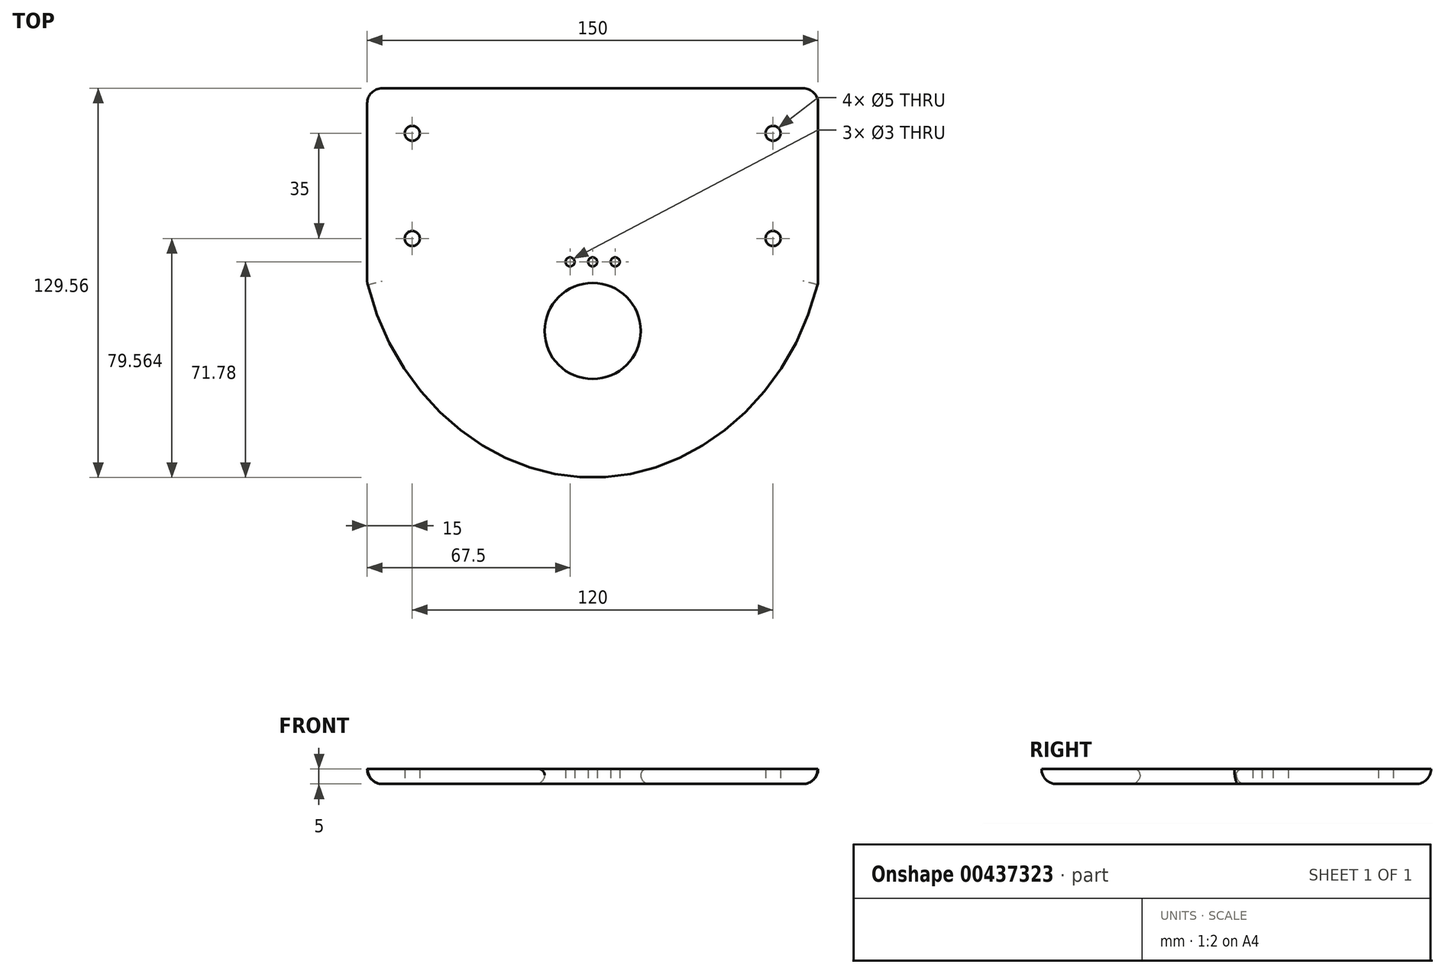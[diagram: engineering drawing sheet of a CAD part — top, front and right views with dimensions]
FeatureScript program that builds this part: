
annotation { "Feature Type Name" : "Feature", "Feature Type Description" : "" }
export const myFeature = defineFeature(function(context is Context, id is Id, definition is map)
    precondition{}
    {
        {
            var Q0;
            Q0=qCreatedBy(makeId("Top.planeOp"),FACE);
            var sketch = newSketch(context, id + "F0", { "sketchPlane" : qUnion([Q0])});
            skLineSegment(sketch, "E0.bottom", {"start": v(75, 64.78) * mm, "end": v(-75, 64.78) * mm});
            skLineSegment(sketch, "E0.top", {"start": v(0, -64.78) * mm, "end": v(0, -64.78) * mm});
            skLineSegment(sketch, "E0.left", {"start": v(75, 64.78) * mm, "end": v(75, 0) * mm});
            skLineSegment(sketch, "E0.right", {"start": v(-75, 64.78) * mm, "end": v(-75, 0) * mm});
            skPoint(sketch, "E0.middle", {"position": v(0, 0) * mm});
            skLineSegment(sketch, "E1", {"start": v(0, 64.78) * mm, "end": v(0, -64.78) * mm, "construction": true});
            skLineSegment(sketch, "E2", {"start": v(-75, 0) * mm, "end": v(100.62, 0) * mm, "construction": true});
            skPoint(sketch, "E2.startSnap0", {"position": v(-75, 0) * mm});
            skPoint(sketch, "E3.orphan", {"position": v(-130.6, 0) * mm});
            skFitSpline(sketch, "E4", {"points": [v(-75, 0) * mm, v(0, -64.78) * mm, v(75, 0) * mm], "startDerivative": vector(60, -240) * mm, "endDerivative": vector(60, 240) * mm});
            skPoint(sketch, "E5.orphan", {"position": v(-75, -64.78) * mm});
            skPoint(sketch, "E6.orphan", {"position": v(75, -64.78) * mm});
            skCircle(sketch, "E7", {"center": v(60, 49.78) * mm, "radius": 2.5 * mm});
            skCircle(sketch, "E8", {"center": v(60, 14.78) * mm, "radius": 2.5 * mm});
            skCircle(sketch, "E9.MirrorC", {"center": v(-60, 14.78) * mm, "radius": 2.5 * mm});
            skCircle(sketch, "E10.MirrorC", {"center": v(-60, 49.78) * mm, "radius": 2.5 * mm});
            skCircle(sketch, "E11", {"center": v(0, 7) * mm, "radius": 1.5 * mm});
            skCircle(sketch, "E12", {"center": v(7.5, 7) * mm, "radius": 1.5 * mm});
            skCircle(sketch, "E13", {"center": v(-7.5, 7) * mm, "radius": 1.5 * mm});
            skSolve(sketch);
        }
        {
            var Q0;
            Q0=makeQuery(id+"F0.imprint","IMPRINT",FACE,{"disambiguationData":[TD([[makeQuery(id+"F0.imprint","IMPRINT",EDGE,{"derivedFrom":sQuery(id+"F0.wireOp",EDGE,"E0.bottom")}),1.0]])]});
            var sketch = newSketch(context, id + "F1", { "sketchPlane" : qUnion([Q0])});
            skCircle(sketch, "E14", {"center": v(0, -16) * mm, "radius": 16 * mm});
            skSolve(sketch);
        }
        {
            var Q0;
            Q0=makeQuery(id+"F1.imprint","IMPRINT",FACE,{"disambiguationData":[TD([[makeQuery(id+"F1.imprint","IMPRINT",EDGE,{"derivedFrom":sQuery(id+"F1.wireOp",EDGE,"E14")}),-1.0]])]});
            extrude(context, id + "F2", {"entities" : qUnion([Q0]), "depth" : 5 * mm});
        }
        {
            var Q0;
            Q0=makeQuery(id+"F2.opExtrude","CAP_EDGE",EDGE,{"disambiguationData":[OSD([sQuery(id+"F0.wireOp",EDGE,"E4")])],"isStart":true});
            fillet(context, id + "F3", {"entities" : qUnion([Q0]), "radius" : 5 * mm, "tangentPropagation" : true, "allowEdgeOverflow" : false});
        }
        {
            var Q0;
            Q0=makeQuery(id+"F2.opExtrude","CAP_EDGE",EDGE,{"disambiguationData":[OSD([sQuery(id+"F1.wireOp",EDGE,"E14")])],"isStart":true});
            fillet(context, id + "F4", {"entities" : qUnion([Q0]), "radius" : 3 * mm, "tangentPropagation" : true, "allowEdgeOverflow" : false});
        }
        {
            var Q0;
            Q0=makeQuery(id+"F2.opExtrude","CAP_EDGE",EDGE,{"disambiguationData":[OSD([sQuery(id+"F1.wireOp",EDGE,"E14")])],"isStart":false});
            fillet(context, id + "F5", {"entities" : qUnion([Q0]), "radius" : 2 * mm, "tangentPropagation" : true, "allowEdgeOverflow" : false});
        }
        {
            var Q0;
            Q0=makeQuery(id+"F2.opExtrude","CAP_EDGE",EDGE,{"disambiguationData":[OSD([sQuery(id+"F0.wireOp",EDGE,"E0.bottom")])],"isStart":true});
            fillet(context, id + "F6", {"entities" : qUnion([Q0]), "radius" : 5 * mm, "tangentPropagation" : true, "allowEdgeOverflow" : false});
        }
        {
            var Q0;
            Q0=makeQuery(id+"F2.opExtrude","CAP_EDGE",EDGE,{"disambiguationData":[OSD([sQuery(id+"F0.wireOp",EDGE,"E0.right")])],"isStart":true});
            fillet(context, id + "F7", {"entities" : qUnion([Q0]), "radius" : 5 * mm, "tangentPropagation" : true, "allowEdgeOverflow" : false});
        }
        {
            var Q0;
            Q0=makeQuery(id+"F2.opExtrude","CAP_EDGE",EDGE,{"disambiguationData":[OSD([sQuery(id+"F0.wireOp",EDGE,"E0.left")])],"isStart":true});
            fillet(context, id + "F8", {"entities" : qUnion([Q0]), "radius" : 5 * mm, "tangentPropagation" : true, "allowEdgeOverflow" : false});
        }
    });
